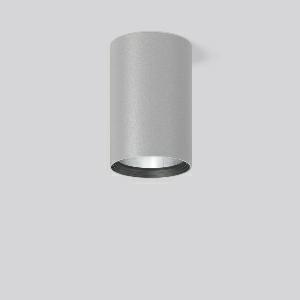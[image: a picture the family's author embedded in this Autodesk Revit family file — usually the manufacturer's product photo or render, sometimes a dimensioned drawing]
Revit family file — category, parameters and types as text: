
# Revit family: heledon_maxi_a_931231_004_10a2
name_source: partatom
category: Lighting Fixtures
units: mm (PartAtom-declared; Revit-internal decimal feet)

## family parameters
Cut with Voids When Loaded = No
Host = Face
Light Source = No
Part Type = Normal
Room Calculation Point = No
Round Connector Dimension = Use Diameter
Shared = No

## types (1)
- HELEDON maxi A (1 x LED Modul 932 fresh meat, 2150 lm, 3200)
    Apparent Load = 33 VA
    Approval mark = CE
    CIE Flux Codes = 100 100 100 100 100
    Color Rendering = 90
    Color Temperature = 3200
    Default Elevation = 1800 mm
    Description = Series: HELEDON maxi
Cylindrical surface-mounted downlight. Housing: die-cast aluminium, powder-coated. Internal ceiling frame polycarbonate with bayonet mounting. Black plastic ring and recessed LED to prevent glare from the side. Optical assembly with reflector made of MIRO-Silver with 98% total light reflection for outstanding efficiency - can be changed without tools. Special LED for illumination of meat included. Suitable for Ceiling mounting. Easy installation with a separate ceiling frame with bayonet mounting and plug connection. Driver integrated. Connected via plug-in connector. High quality converter without flickering and stroboscopic effect. The following accessories can be mounted without use of tools: interchangeable lenses, decorative glasses, honeycomb louvre, clear and frosted diffusers, white interchangeable plastic ring. 
Colour: silver
Diameter: 123 mm
Height: 183 mm
Lamp: LED
Socket: without socket
Colour temperature: fresh meat
System power: 33 W
Rated luminous flux: 2150 lm
Luminous efficiency: 65 lm/W
Control gear: Regulated power supply
Protection class: I
Type of protection: IP 20
    Height = 183 mm
    Lamp = 1 x LED Modul 932 fresh meat
    Lamp Light Flux = 2150 lm
    Lamp count = 1
    Length = 123 mm
    Lifetime = 50000 h
    Luminous efficacy = 65 lm/W
    Manufacturer = RZB
    ModVariant = No
    Model = 931231.004
    Mounting Place = Ceiling
    Mounting Type = Surface mounted
    Number of Poles = 1
    OnlyDefault = Yes
    Power Factor = 1
    Product Name = HELEDON maxi A
    Product group = Surface mounted downlights
    ProductGroupID = 302
    Protection Class = Protection class I
    Protection Degree = IP 20
    RLX_Detail_Level = 1
    RLX_Emergency_Light_Flux = 0 lm
    RLX_Emergency_Type = 0
    RLX_Emergency_Type_DB = No
    RlxData = <blob elided: 99121 chars, md5=7cddf4c6>
    Socket = socket
    Standby Power = 0 W
    System Light Flux = 2150 lm
    System Power = 33 W
    Type Comments = Product without accessories
    Type Image = 931192.004.jpg
    URL = http://relux.com
    VarID = ---
    Voltage = 230 V
    Voltage Range = 220-240 V
    Weight = 0.00 kg
    Width = 0 mm  [stored 0 ft]

note: [stored X ft] marks values corroborated as IEEE doubles in the binary element streams (Revit-internal decimal feet)

## geometry (parser evidence)
native form markers: Blend x4, Sweep x9
no freeform markers — native parametric forms only
